# Revit family: 634-00-001 DN50-80
name_source: partatom
category: Pipe Accessories
units: mm (PartAtom-declared; Revit-internal decimal feet)

## family parameters
Always vertical = Yes
Cut with Voids When Loaded = No
Part Type = Valve - Breaks Into
Round Connector Dimension = Use Diameter
Shared = No
Work Plane-Based = No

## types (14) — shared parameters
10 = 10 mm  [stored 0.0328084 ft]
2 = 2 mm  [stored 0.00656168 ft]
DN50_PN16_AVK ref. no. 634-071-00-016 = 634-071-00-016
DN50_PN16_AVK ref. no. 634-071-01-016 = 634-071-01-016
DN50_PN16_AVK ref. no. 634-071-01-026 = 634-071-01-026
DN50_PN16_AVK ref. no. 634-071-01-036 = 634-071-01-036
DN50_PN16_AVK ref. no. 634-071-01-046 = 634-071-01-046
DN50_PN16_AVK ref. no. 634-071-01-056 = 634-071-01-056
DN50_PN16_AVK ref. no. 634-071-01-066 = 634-071-01-066
DN65_PN16_AVK ref. no. 634-091-00-016 = 634-091-00-016
DN65_PN16_AVK ref. no. 634-091-00-036 = 634-091-00-036
DN65_PN16_AVK ref. no. 634-091-01-016 = 634-091-01-036
DN65_PN16_AVK ref. no. 634-091-01-056 = 634-091-01-056
DN65_PN16_AVK ref. no. 634-091-01-066 = 634-091-01-066
DN80_PN16_AVK ref. no. 634-106-00-016 = 634-106-00-016
DN80_PN16_AVK ref. no. 634-106-00-036 = 634-106-00-036
Description_ = AVK SUPA MAXI™ END CAP, PN16
FL_T = 19 mm  [stored 0.062336 ft]
L-L1 = 41 mm  [stored 0.134514 ft]
Search_table = 634-00-001 DN50_80
URL product pages = https://www.avkvalves.com
zero-valued in all types: Default Elevation, Thickness

## per-type parameters (varying)
| type | Bolt_L | Bore | D | D-10 | D1 | D11 | D12 | D1_L | D2 | D2_L | DN | L | L1 | Nut | Radius | S1 | S2 |
| DN50_PN16_AVK ref. no. 634-071-00-016 | 54 mm  [stored 0.177165 ft] | 25 mm  [stored 0.082021 ft] | 100 mm | 90 mm  [stored 0.295276 ft] | 44 mm  [stored 0.144357 ft] | 75 mm  [stored 0.246063 ft] | 9 mm  [stored 0.0295276 ft] | 38 mm  [stored 0.124672 ft] | 31 mm  [stored 0.101706 ft] | 68 mm  [stored 0.223097 ft] | 50 mm  [stored 0.164042 ft] | 98 mm | 49 mm  [stored 0.160761 ft] | 14 mm  [stored 0.0459318 ft] | 33 mm  [stored 0.108268 ft] | 24 mm  [stored 0.0787402 ft] | 36 mm |
| DN50_PN16_AVK ref. no. 634-071-01-016 | 54 mm  [stored 0.177165 ft] | 25 mm  [stored 0.082021 ft] | 100 mm | 90 mm  [stored 0.295276 ft] | 44 mm  [stored 0.144357 ft] | 75 mm  [stored 0.246063 ft] | 9 mm  [stored 0.0295276 ft] | 38 mm  [stored 0.124672 ft] | 31 mm  [stored 0.101706 ft] | 68 mm  [stored 0.223097 ft] | 50 mm  [stored 0.164042 ft] | 75 mm  [stored 0.246063 ft] | 38 mm  [stored 0.124672 ft] | 14 mm  [stored 0.0459318 ft] | 33 mm  [stored 0.108268 ft] | 24 mm  [stored 0.0787402 ft] | 36 mm |
| DN50_PN16_AVK ref. no. 634-071-01-026 | 54 mm  [stored 0.177165 ft] | 25 mm  [stored 0.082021 ft] | 100 mm | 90 mm  [stored 0.295276 ft] | 44 mm  [stored 0.144357 ft] | 75 mm  [stored 0.246063 ft] | 9 mm  [stored 0.0295276 ft] | 38 mm  [stored 0.124672 ft] | 31 mm  [stored 0.101706 ft] | 68 mm  [stored 0.223097 ft] | 50 mm  [stored 0.164042 ft] | 75 mm  [stored 0.246063 ft] | 38 mm  [stored 0.124672 ft] | 14 mm  [stored 0.0459318 ft] | 33 mm  [stored 0.108268 ft] | 24 mm  [stored 0.0787402 ft] | 36 mm |
| DN50_PN16_AVK ref. no. 634-071-01-036 | 54 mm  [stored 0.177165 ft] | 25 mm  [stored 0.082021 ft] | 100 mm | 90 mm  [stored 0.295276 ft] | 44 mm  [stored 0.144357 ft] | 75 mm  [stored 0.246063 ft] | 9 mm  [stored 0.0295276 ft] | 38 mm  [stored 0.124672 ft] | 31 mm  [stored 0.101706 ft] | 68 mm  [stored 0.223097 ft] | 50 mm  [stored 0.164042 ft] | 75 mm  [stored 0.246063 ft] | 38 mm  [stored 0.124672 ft] | 14 mm  [stored 0.0459318 ft] | 33 mm  [stored 0.108268 ft] | 24 mm  [stored 0.0787402 ft] | 36 mm |
| DN50_PN16_AVK ref. no. 634-071-01-046 | 54 mm  [stored 0.177165 ft] | 25 mm  [stored 0.082021 ft] | 100 mm | 90 mm  [stored 0.295276 ft] | 44 mm  [stored 0.144357 ft] | 75 mm  [stored 0.246063 ft] | 9 mm  [stored 0.0295276 ft] | 38 mm  [stored 0.124672 ft] | 31 mm  [stored 0.101706 ft] | 68 mm  [stored 0.223097 ft] | 51 mm | 75 mm  [stored 0.246063 ft] | 38 mm  [stored 0.124672 ft] | 14 mm  [stored 0.0459318 ft] | 33 mm  [stored 0.108268 ft] | 24 mm  [stored 0.0787402 ft] | 36 mm |
| DN50_PN16_AVK ref. no. 634-071-01-056 | 54 mm  [stored 0.177165 ft] | 25 mm  [stored 0.082021 ft] | 100 mm | 90 mm  [stored 0.295276 ft] | 44 mm  [stored 0.144357 ft] | 75 mm  [stored 0.246063 ft] | 9 mm  [stored 0.0295276 ft] | 38 mm  [stored 0.124672 ft] | 31 mm  [stored 0.101706 ft] | 68 mm  [stored 0.223097 ft] | 51 mm | 75 mm  [stored 0.246063 ft] | 38 mm  [stored 0.124672 ft] | 14 mm  [stored 0.0459318 ft] | 33 mm  [stored 0.108268 ft] | 24 mm  [stored 0.0787402 ft] | 36 mm |
| DN50_PN16_AVK ref. no. 634-071-01-066 | 54 mm  [stored 0.177165 ft] | 25 mm  [stored 0.082021 ft] | 100 mm | 90 mm  [stored 0.295276 ft] | 44 mm  [stored 0.144357 ft] | 75 mm  [stored 0.246063 ft] | 9 mm  [stored 0.0295276 ft] | 38 mm  [stored 0.124672 ft] | 31 mm  [stored 0.101706 ft] | 68 mm  [stored 0.223097 ft] | 51 mm | 75 mm  [stored 0.246063 ft] | 38 mm  [stored 0.124672 ft] | 14 mm  [stored 0.0459318 ft] | 33 mm  [stored 0.108268 ft] | 24 mm  [stored 0.0787402 ft] | 36 mm |
| DN65_PN16_AVK ref. no. 634-091-00-016 | 54 mm  [stored 0.177165 ft] | 33 mm  [stored 0.108268 ft] | 113 mm | 103 mm | 44 mm  [stored 0.144357 ft] | 85 mm  [stored 0.278871 ft] | 9 mm  [stored 0.0295276 ft] | 38 mm  [stored 0.124672 ft] | 31 mm  [stored 0.101706 ft] | 68 mm  [stored 0.223097 ft] | 65 mm  [stored 0.213255 ft] | 109 mm | 55 mm  [stored 0.180446 ft] | 14 mm  [stored 0.0459318 ft] | 33 mm  [stored 0.108268 ft] | 35 mm  [stored 0.114829 ft] | 46 mm |
| DN65_PN16_AVK ref. no. 634-091-00-036 | 69 mm  [stored 0.226378 ft] | 33 mm  [stored 0.108268 ft] | 113 mm | 103 mm | 52 mm | 85 mm  [stored 0.278871 ft] | 9 mm  [stored 0.0295276 ft] | 48 mm  [stored 0.15748 ft] | 41 mm  [stored 0.134514 ft] | 86 mm  [stored 0.282152 ft] | 65 mm  [stored 0.213255 ft] | 109 mm | 55 mm  [stored 0.180446 ft] | 17 mm | 33 mm  [stored 0.108268 ft] | 35 mm  [stored 0.114829 ft] | 46 mm |
| DN65_PN16_AVK ref. no. 634-091-01-016 | 69 mm  [stored 0.226378 ft] | 33 mm  [stored 0.108268 ft] | 113 mm | 103 mm | 52 mm | 85 mm  [stored 0.278871 ft] | 9 mm  [stored 0.0295276 ft] | 48 mm  [stored 0.15748 ft] | 41 mm  [stored 0.134514 ft] | 86 mm  [stored 0.282152 ft] | 65 mm  [stored 0.213255 ft] | 78 mm | 39 mm | 17 mm | 33 mm  [stored 0.108268 ft] | 35 mm  [stored 0.114829 ft] | 46 mm |
| DN65_PN16_AVK ref. no. 634-091-01-056 | 69 mm  [stored 0.226378 ft] | 33 mm  [stored 0.108268 ft] | 113 mm | 103 mm | 52 mm | 85 mm  [stored 0.278871 ft] | 9 mm  [stored 0.0295276 ft] | 48 mm  [stored 0.15748 ft] | 41 mm  [stored 0.134514 ft] | 86 mm  [stored 0.282152 ft] | 65 mm  [stored 0.213255 ft] | 78 mm | 39 mm | 17 mm | 33 mm  [stored 0.108268 ft] | 35 mm  [stored 0.114829 ft] | 46 mm |
| DN65_PN16_AVK ref. no. 634-091-01-066 | 69 mm  [stored 0.226378 ft] | 33 mm  [stored 0.108268 ft] | 113 mm | 103 mm | 52 mm | 85 mm  [stored 0.278871 ft] | 9 mm  [stored 0.0295276 ft] | 48 mm  [stored 0.15748 ft] | 41 mm  [stored 0.134514 ft] | 86 mm  [stored 0.282152 ft] | 66 mm | 78 mm | 39 mm | 17 mm | 33 mm  [stored 0.108268 ft] | 35 mm  [stored 0.114829 ft] | 46 mm |
| DN80_PN16_AVK ref. no. 634-106-00-016 | 69 mm  [stored 0.226378 ft] | 40 mm | 118 mm | 108 mm | 63 mm | 88 mm  [stored 0.288714 ft] | 10 mm  [stored 0.0328084 ft] | 49 mm  [stored 0.160761 ft] | 41 mm  [stored 0.134514 ft] | 86 mm  [stored 0.282152 ft] | 80 mm | 110 mm | 55 mm  [stored 0.180446 ft] | 17 mm | 35 mm  [stored 0.114829 ft] | 41 mm  [stored 0.134514 ft] | 53 mm  [stored 0.173885 ft] |
| DN80_PN16_AVK ref. no. 634-106-00-036 | 69 mm  [stored 0.226378 ft] | 40 mm | 118 mm | 108 mm | 63 mm | 88 mm  [stored 0.288714 ft] | 10 mm  [stored 0.0328084 ft] | 49 mm  [stored 0.160761 ft] | 41 mm  [stored 0.134514 ft] | 86 mm  [stored 0.282152 ft] | 80 mm | 110 mm | 55 mm  [stored 0.180446 ft] | 17 mm | 35 mm  [stored 0.114829 ft] | 41 mm  [stored 0.134514 ft] | 53 mm  [stored 0.173885 ft] |

note: [stored X ft] marks values corroborated as IEEE doubles in the binary element streams (Revit-internal decimal feet)

## geometry (parser evidence)
native form markers: Sweep x4
no freeform markers — native parametric forms only
